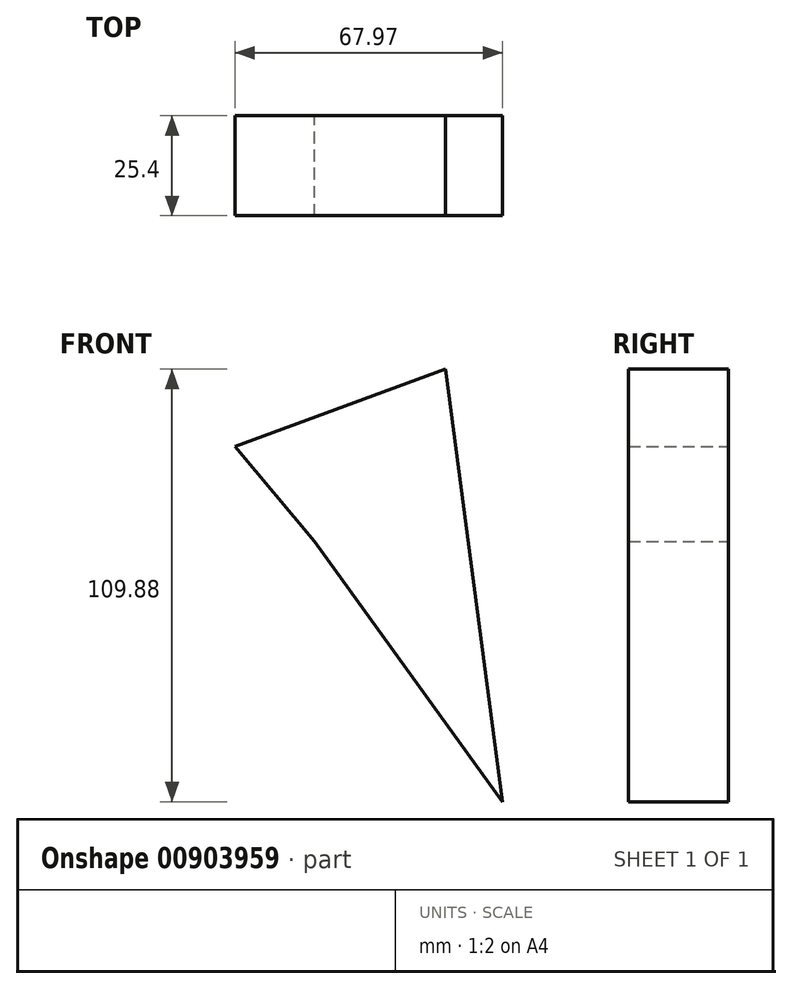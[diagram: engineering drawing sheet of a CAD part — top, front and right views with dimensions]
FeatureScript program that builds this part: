
annotation { "Feature Type Name" : "Feature", "Feature Type Description" : "" }
export const myFeature = defineFeature(function(context is Context, id is Id, definition is map)
    precondition{}
    {
        {
            var Q0;
            Q0=qCreatedBy(makeId("Front.planeOp"),FACE);
            var sketch = newSketch(context, id + "F0", { "sketchPlane" : qUnion([Q0])});
            skLineSegment(sketch, "E0", {"start": v(-20.2, 24.17) * mm, "end": v(0, 0) * mm});
            skLineSegment(sketch, "E1", {"start": v(0, 0) * mm, "end": v(47.77, -66.08) * mm});
            skLineSegment(sketch, "E2", {"start": v(47.77, -66.08) * mm, "end": v(33.23, 43.8) * mm});
            skLineSegment(sketch, "E3", {"start": v(33.23, 43.8) * mm, "end": v(-20.2, 24.17) * mm});
            skSolve(sketch);
        }
        {
            var Q0;
            Q0 = qSketchRegion(id + "F0", true);
            var Q1;
            Q1=sQuery(id+"F0.wireOp",EDGE,"E3");
            extrude(context, id + "F1", {"entities" : qUnion([Q0]), "surfaceOperationType" : NewSurfaceOperationType.ADD, "surfaceEntities" : qUnion([Q1]), "endBound" : BoundingType.SYMMETRIC, "depth" : 25.4 * mm, "offsetDistance" : 25.4 * mm});
        }
    });
